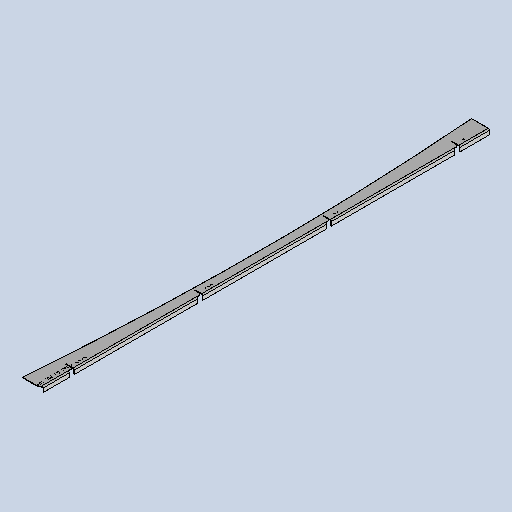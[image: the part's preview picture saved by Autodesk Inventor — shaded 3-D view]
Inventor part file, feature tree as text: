
AUTODESK INVENTOR PART (.ipt)
format: ipt  version: 2025 (Build 290162010, 162A)  size: 532,992 bytes
history: native  units: mm
features: other x6, sheet_metal_op x4, sketch x4, extrude x1, pattern_linear x1, projected_geometry x1
ambient origin geometry x8: Origin, YZ Plane, XZ Plane, XY Plane, X Axis, Y Axis, Z Axis, Center Point
bodies: Body1 (feature_tree)
feature tree (17):
  sheet_metal_op  "Face2"
  sheet_metal_op  "Flange2"
  extrude  "Extrusion2"  Depth=2.0mm
  pattern_linear  "Rectangular Pattern3"  Spacing1=2.75mm  [1 undecoded]
  other  "Mark1"
  other  "Corner Chamfer1"
  other  "A-Side Definition"
  sketch  "Sketch1"  dims[d25=50.0mm d33=50.0mm d46=2.0mm]
  other  "Plate3"
  sketch  "Sketch3"  dims[d47=2.0mm]
  other  "Plate4"
  sheet_metal_op  "Bend2"
  sheet_metal_op  "Corner2"
  sketch  "Sketch5"  dims[d48=1.0mm]
  projected_geometry  "Projected Loop2"
  sketch  "Sketch6"  dims[d49=4.0mm d50=2.75mm d51=20.0mm d52=90.0deg d53=2.75mm d54=8.0mm d55=2.0mm d56=2.75mm d57=500.0mm d58=500.0mm d59=500.0mm d60=500.0mm d61=500.0mm d69=1735.171219mm d70=2.0mm d71=0.0mm d72=0.0mm d76=61.625948mm d79=30.0mm d80=39.195636mm d102=62.276234mm d104=39.411954mm d106=2.0mm d107=20.0mm d108=116.0mm d112=31.0mm d113=40.0mm d115=500.0mm d120=200.0mm d121=12.0mm d123=5.0mm d126=50.0mm d127=25.0mm d135=25.0mm d136=25.0mm d137=25.0mm d141=1745.171mm d142=500.0mm d143=500.0mm d144=500.0mm d145=6.0mm d146=6.0mm d147=45.0deg d148=70.0mm d149=11053.0mm d150=71.959mm d151=23.736478mm d153=10.0mm]
  other  "Definition1"
note: 1 required parameter value undecoded (feature->parameter linkage not recoverable at this tier; creation-order binding heuristic only, values carry confidence <= 0.55)
